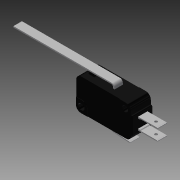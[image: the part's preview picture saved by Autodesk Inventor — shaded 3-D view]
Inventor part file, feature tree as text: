
AUTODESK INVENTOR PART (.ipt)
format: ipt  version: 2014 (Build 180170000, 170)  size: 337,920 bytes
history: native  units: in
note: dims shown in document units (in); Inventor stores cm internally (conversion verified against a paired STEP export)
features: extrude x6, sketch x2, hole x2
ambient origin geometry x8: Origin, YZ Plane, XZ Plane, XY Plane, X Axis, Y Axis, Z Axis, Center Point
bodies: Solid1 (feature_tree)
feature tree (10):
  sketch  "Sketch1"  dims[d0=0.8749in d1=0.8749in d2=1.135in d3=1.135in]
  extrude  "Extrusion1"  Depth=1.135in
  sketch  "Sketch2"  dims[d4=0.4054in d5=0.4054in d6=0.17in d7=0.0in d8=0.3854in d9=0.3854in d10=0.6024in d11=0.6024in d12=0.402in d13=0.402in d14=0.24in d15=0.24in d16=0.6529in d17=0.6529in d18=2.3471in d19=2.3471in d20=0.02in d21=0.02in d22=0.125in d23=0.125in d24=0.187in d25=0.187in d26=0.126in d27=0.126in d28=0.235in d29=0.235in d30=0.0104in d31=0.0104in d32=0.54in d33=0.54in d34=0.323in d35=0.323in d36=0.114in d37=0.114in d38=0.11in d39=0.11in d40=0.116in d41=0.116in d42=0.626in d43=0.626in d44=0.04in d45=0.04in d46=0.386in d47=0.0in d48=0.402in d49=0.0in d50=0.402in d51=0.0in d52=0.15in d53=0.0in d54=0.17in d55=0.0in d56=0.187in d57=0.0in d58=0.125in d59=0.0935in d60=0.055in d61=0.5in d62=0.375in d63=0.25in d64=0.5635in d65=0.75in d66=0.8108in d67=0.0935in d68=0.125in d69=0.055in d70=0.5in d71=0.375in d72=0.25in d73=0.5635in d74=0.75in d75=0.8108in]
  extrude  "Extrusion2"  Depth=0.17in TaperAngle=0.0deg
  extrude  "Extrusion3"  Depth=0.187in
  extrude  "Extrusion4"  Depth=0.187in
  extrude  "Extrusion5"  Depth=0.402in
  extrude  "Extrusion6"  Depth=0.24in
  hole  "Hole1"  [1 undecoded]
  hole  "Hole2"  [1 undecoded]
note: 2 required parameter values undecoded (feature->parameter linkage not recoverable at this tier; creation-order binding heuristic only, values carry confidence <= 0.55)
